# Revit family: CL 50 Gourmet (a)
name_source: partatom
category: Equipement spécialisé
revit_build: Autodesk Revit LT 2015 (Build: 20140606_1530(x64)
units: mm (PartAtom-declared; Revit-internal decimal feet)

## types (5) — shared parameters
Apparent Power = 0 VA
Depth = 311 mm
Description = COUPE-LEGUMES
Electrique connexion = 133 mm
Fabricant = ROBOT COUPE
Height = 595 mm
Modèle = CL50 Gourmet
UP Depth = 586 mm
UP Height = 746 mm
URL = www.robot-coupe.com
Width = 377 mm
water = Connector
zero-valued in all types: Cold water supply height, Top, Waste water height

## per-type parameters (varying)
| type | Amps | Cycle | HP | Phase | Speeds (Rpm) | Volts | Watts | Weight |
| CL50 Gourmet  120/60/1 | 12 A | 60 Hz |  | 1 | 375 | 120 V | 550 W | 21.5 kg |
| CL50 Gourmet  220/60/1 | 4 A | 60 Hz |  | 1 | 375 | 220 V | 550 W | 21.5 kg |
| CL50 Gourmet  220-240/50/1 | 5.7 A | 50 Hz |  | 1 | 375 | 240 V | 550 W | 21.5 kg |
| CL50 Gourmet  400/50/3 | 1.9 A | 50 Hz |  | 3 | 375 | 400 V | 600 W | 21.5 kg |
| CL50 Gourmet USA  120/60/1 | 13.5 A | 60 Hz | 1.5 | 1 | 425 | 120 V | 0 W | 51 lbs |

## geometry (parser evidence)
native form markers: Blend x104, Sweep x4
no freeform markers — native parametric forms only
